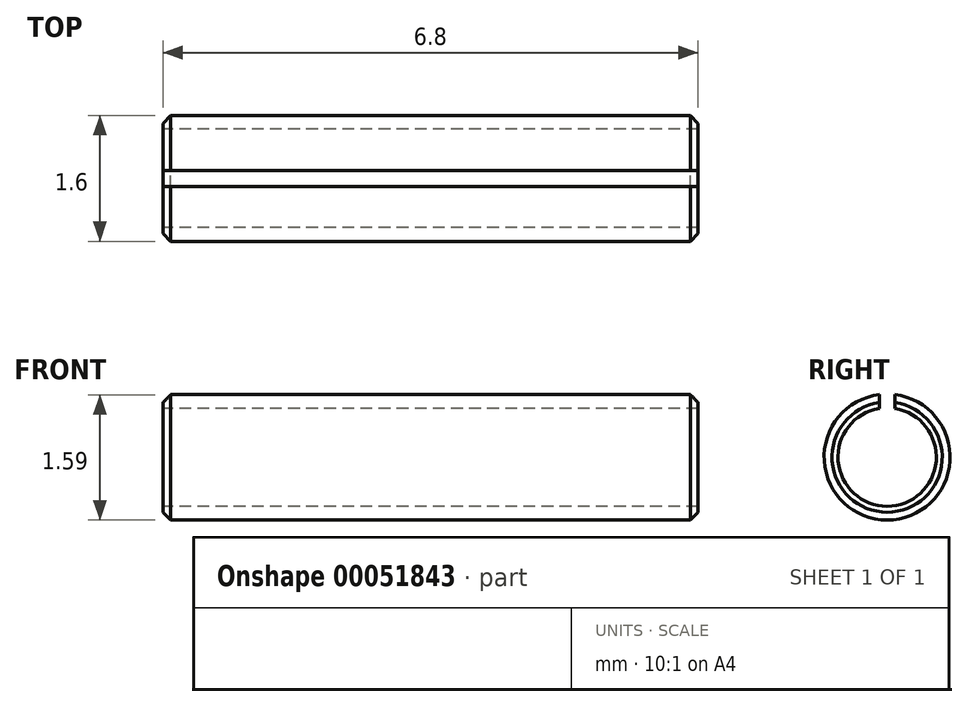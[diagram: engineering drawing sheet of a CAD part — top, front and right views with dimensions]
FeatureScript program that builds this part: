
annotation { "Feature Type Name" : "Feature", "Feature Type Description" : "" }
export const myFeature = defineFeature(function(context is Context, id is Id, definition is map)
    precondition{}
    {
        {
            var Q0;
            Q0=qCreatedBy(makeId("Right.planeOp"),FACE);
            var sketch = newSketch(context, id + "F0", { "sketchPlane" : qUnion([Q0])});
            skArc(sketch, "E0", {"start": v(-0.1, 0.62) * mm, "mid": v(0, -0.62) * mm, "end": v(0.1, 0.62) * mm});
            skArc(sketch, "E1", {"start": v(-0.1, 0.8) * mm, "mid": v(0, -0.8) * mm, "end": v(0.1, 0.8) * mm});
            skLineSegment(sketch, "E2", {"start": v(0.1, 0.62) * mm, "end": v(0.1, 0.8) * mm});
            skLineSegment(sketch, "E3", {"start": v(-0.1, 0.8) * mm, "end": v(-0.1, 0.62) * mm});
            skPoint(sketch, "E4.start.orphan", {"position": v(-0.1, 0) * mm});
            skSolve(sketch);
        }
        {
            var Q0;
            Q0 = qSketchRegion(id + "F0", true);
            extrude(context, id + "F1", {"entities" : qUnion([Q0]), "depth" : 6.8 * mm});
        }
        {
            var Q0;
            Q0=makeQuery(id+"F1.opExtrude","CAP_EDGE",EDGE,{"disambiguationData":[OSD([sQuery(id+"F0.wireOp",EDGE,"E1")])],"isStart":false});
            chamfer(context, id + "F2", {"entities" : qUnion([Q0]), "width" : .1 * mm});
        }
        {
            var Q0;
            Q0=makeQuery(id+"F1.opExtrude","CAP_EDGE",EDGE,{"disambiguationData":[OSD([sQuery(id+"F0.wireOp",EDGE,"E1")])],"isStart":true});
            chamfer(context, id + "F3", {"entities" : qUnion([Q0]), "width" : .1 * mm});
        }
    });
